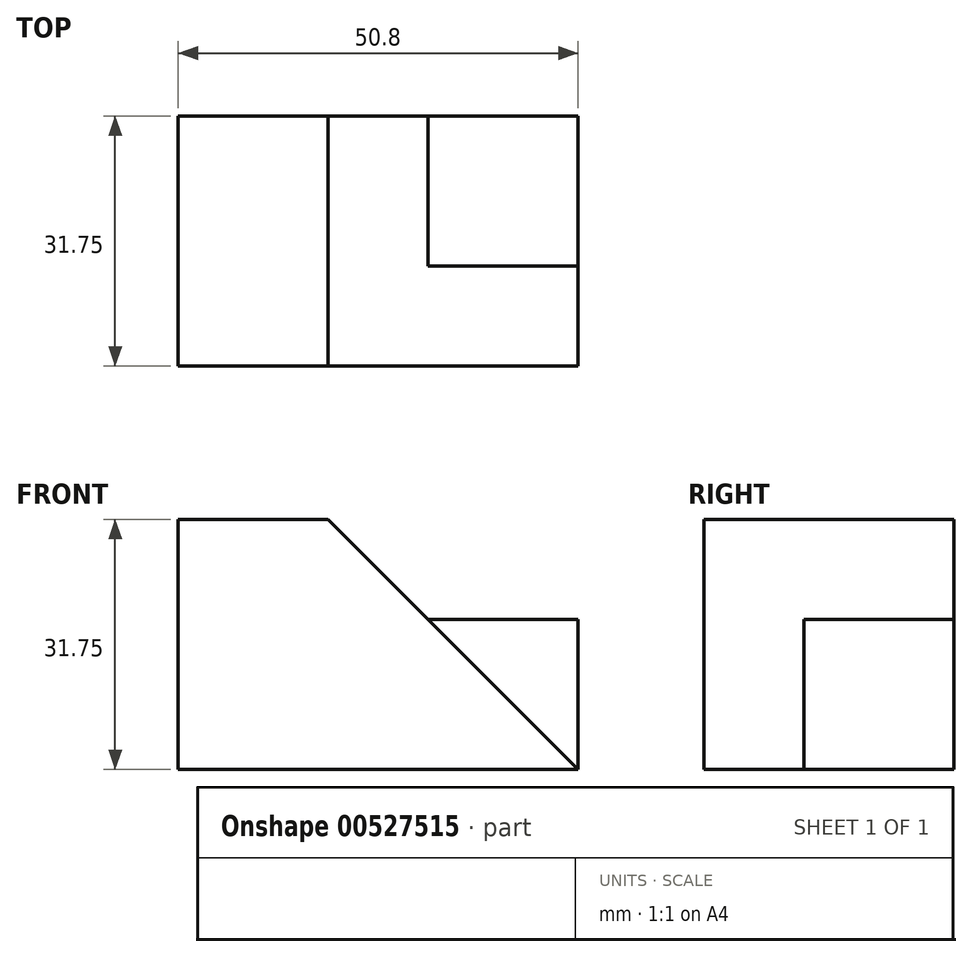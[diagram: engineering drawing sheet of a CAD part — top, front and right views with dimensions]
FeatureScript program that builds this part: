
annotation { "Feature Type Name" : "Feature", "Feature Type Description" : "" }
export const myFeature = defineFeature(function(context is Context, id is Id, definition is map)
    precondition{}
    {
        {
            var Q0;
            Q0=qCreatedBy(makeId("Front.planeOp"),FACE);
            var sketch = newSketch(context, id + "F0", { "sketchPlane" : qUnion([Q0])});
            skLineSegment(sketch, "E0", {"start": v(0, 0) * mm, "end": v(50.8, 0) * mm});
            skLineSegment(sketch, "E1", {"start": v(50.8, 0) * mm, "end": v(50.8, 31.75) * mm});
            skLineSegment(sketch, "E2", {"start": v(50.8, 31.75) * mm, "end": v(0, 31.75) * mm});
            skLineSegment(sketch, "E3", {"start": v(0, 31.75) * mm, "end": v(0, 0) * mm});
            skSolve(sketch);
        }
        {
            var Q0;
            Q0=makeQuery(id+"F0.imprint","IMPRINT",FACE,{"disambiguationData":[TD([[makeQuery(id+"F0.imprint","IMPRINT",EDGE,{"derivedFrom":sQuery(id+"F0.wireOp",EDGE,"E0")}),1.0]])]});
            extrude(context, id + "F1", {"entities" : qUnion([Q0]), "depth" : 31.75 * mm, "offsetDistance" : 25.4 * mm});
        }
        {
            var Q0;
            Q0=makeQuery(id+"F1.opExtrude","CAP_FACE",FACE,{"disambiguationData":[OSD([sQuery(id+"F0.wireOp",EDGE,"E0"),sQuery(id+"F0.wireOp",EDGE,"E1"),sQuery(id+"F0.wireOp",EDGE,"E2"),sQuery(id+"F0.wireOp",EDGE,"E3")])],"isStart":false});
            var sketch = newSketch(context, id + "F2", { "sketchPlane" : qUnion([Q0])});
            skLineSegment(sketch, "E4", {"start": v(0, 0) * mm, "end": v(19.05, 0) * mm});
            skLineSegment(sketch, "E5", {"start": v(19.05, 0) * mm, "end": v(19.05, 31.75) * mm});
            skLineSegment(sketch, "E6", {"start": v(19.05, 31.75) * mm, "end": v(0, 31.75) * mm});
            skLineSegment(sketch, "E7", {"start": v(0, 31.75) * mm, "end": v(0, 0) * mm});
            skLineSegment(sketch, "E8", {"start": v(19.05, 31.75) * mm, "end": v(50.8, 0) * mm});
            skLineSegment(sketch, "E9", {"start": v(50.8, 0) * mm, "end": v(50.8, 31.75) * mm});
            skLineSegment(sketch, "E10", {"start": v(50.8, 31.75) * mm, "end": v(19.05, 31.75) * mm});
            skSolve(sketch);
        }
        {
            var Q0;
            Q0=makeQuery(id+"F2.imprint","IMPRINT",FACE,{"disambiguationData":[TD([[makeQuery(id+"F2.imprint","IMPRINT",EDGE,{"derivedFrom":sQuery(id+"F2.wireOp",EDGE,"E8")}),1.0]])]});
            extrude(context, id + "F3", {"entities" : qUnion([Q0]), "operationType" : NewBodyOperationType.REMOVE, "oppositeDirection" : true, "depth" : 31.75 * mm, "offsetDistance" : 25.4 * mm});
        }
        {
            var Q0;
            Q0=makeQuery(id+"F1.opExtrude","CAP_FACE",FACE,{"disambiguationData":[OSD([sQuery(id+"F0.wireOp",EDGE,"E0"),sQuery(id+"F0.wireOp",EDGE,"E1"),sQuery(id+"F0.wireOp",EDGE,"E2"),sQuery(id+"F0.wireOp",EDGE,"E3")])],"isStart":true});
            var sketch = newSketch(context, id + "F4", { "sketchPlane" : qUnion([Q0])});
            skLineSegment(sketch, "E11", {"start": v(-50.8, 0) * mm, "end": v(-50.8, 19.05) * mm});
            skLineSegment(sketch, "E12", {"start": v(-31.75, 19.05) * mm, "end": v(-50.8, 19.05) * mm});
            skLineSegment(sketch, "E13", {"start": v(-50.8, 0) * mm, "end": v(-31.75, 19.05) * mm});
            skSolve(sketch);
        }
        {
            var Q0;
            Q0=makeQuery(id+"F4.imprint","IMPRINT",FACE,{"disambiguationData":[TD([[makeQuery(id+"F4.imprint","IMPRINT",EDGE,{"derivedFrom":sQuery(id+"F4.wireOp",EDGE,"E11")}),-1.0]])]});
            extrude(context, id + "F5", {"entities" : qUnion([Q0]), "operationType" : NewBodyOperationType.ADD, "oppositeDirection" : true, "depth" : 19.05 * mm, "offsetDistance" : 25.4 * mm});
        }
    });
